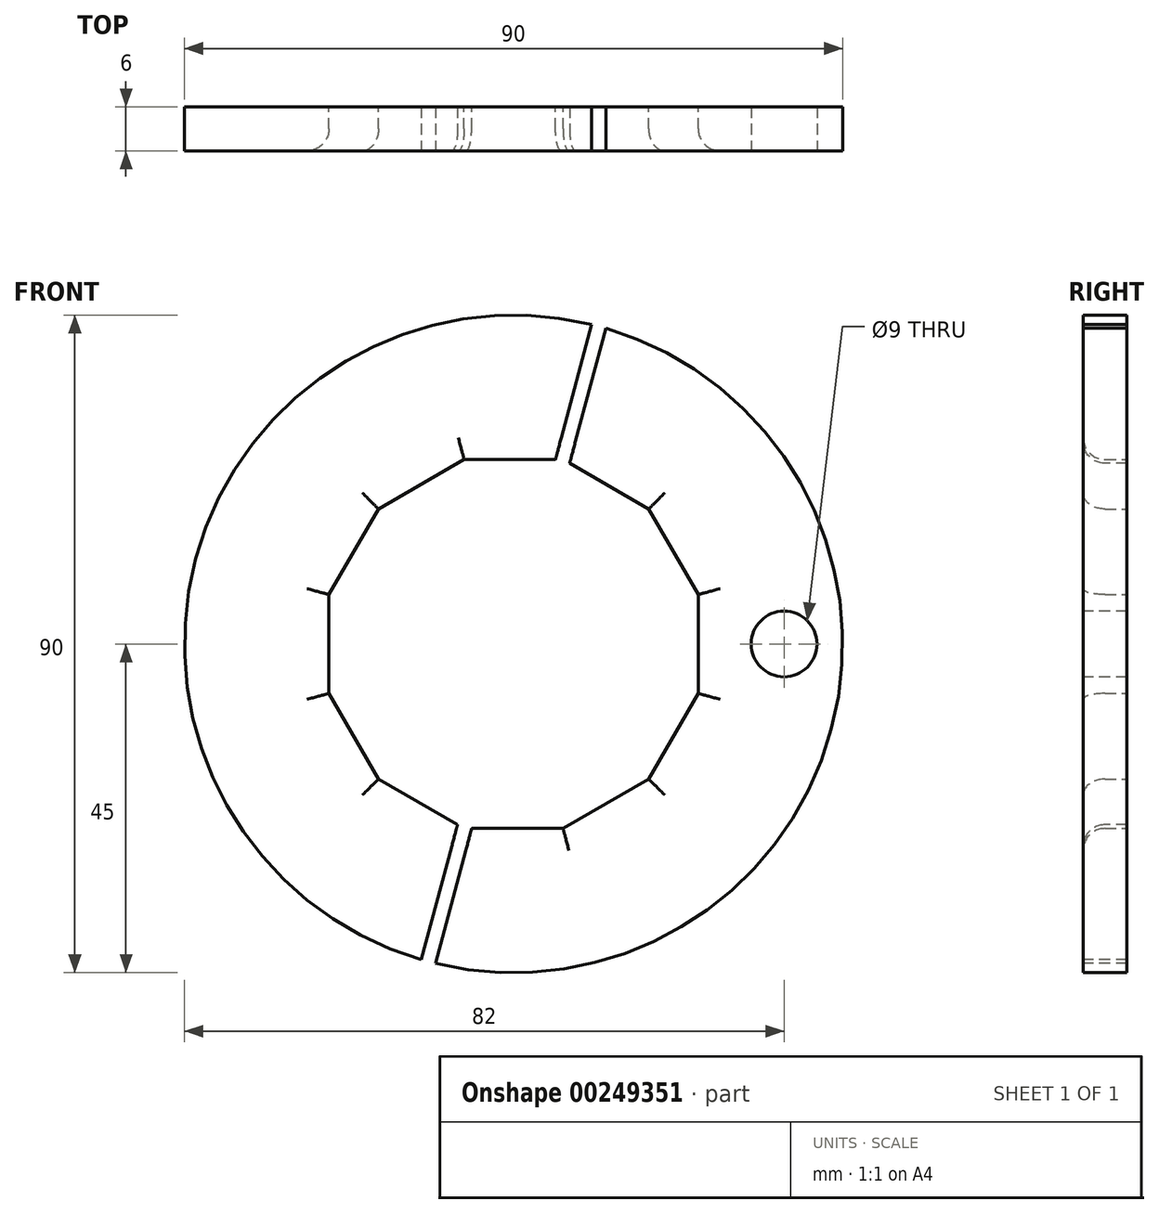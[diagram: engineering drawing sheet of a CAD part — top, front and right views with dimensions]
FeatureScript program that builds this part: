
annotation { "Feature Type Name" : "Feature", "Feature Type Description" : "" }
export const myFeature = defineFeature(function(context is Context, id is Id, definition is map)
    precondition{}
    {
        {
            var Q0;
            Q0=qCreatedBy(makeId("Front.planeOp"),FACE);
            var sketch = newSketch(context, id + "F0", { "sketchPlane" : qUnion([Q0])});
            skCircle(sketch, "E0.cCircle", {"center": v(0, 0) * mm, "radius": 25.25 * mm, "construction": true});
            skLineSegment(sketch, "E0.0", {"start": v(-6.77, 25.25) * mm, "end": v(6.77, 25.25) * mm});
            skLineSegment(sketch, "E0.1", {"start": v(6.77, 25.25) * mm, "end": v(18.48, 18.48) * mm});
            skLineSegment(sketch, "E0.2", {"start": v(18.48, 18.48) * mm, "end": v(25.25, 6.77) * mm});
            skLineSegment(sketch, "E0.3", {"start": v(25.25, 6.77) * mm, "end": v(25.25, -6.77) * mm});
            skLineSegment(sketch, "E0.4", {"start": v(25.25, -6.77) * mm, "end": v(18.48, -18.48) * mm});
            skLineSegment(sketch, "E0.5", {"start": v(18.48, -18.48) * mm, "end": v(6.77, -25.25) * mm});
            skLineSegment(sketch, "E0.6", {"start": v(6.77, -25.25) * mm, "end": v(-6.77, -25.25) * mm});
            skLineSegment(sketch, "E0.7", {"start": v(-6.77, -25.25) * mm, "end": v(-18.48, -18.48) * mm});
            skLineSegment(sketch, "E0.8", {"start": v(-18.48, -18.48) * mm, "end": v(-25.25, -6.77) * mm});
            skLineSegment(sketch, "E0.9", {"start": v(-25.25, -6.77) * mm, "end": v(-25.25, 6.77) * mm});
            skLineSegment(sketch, "E0.10", {"start": v(-25.25, 6.77) * mm, "end": v(-18.48, 18.48) * mm});
            skLineSegment(sketch, "E0.11", {"start": v(-18.48, 18.48) * mm, "end": v(-6.77, 25.25) * mm});
            skPoint(sketch, "E0.0.midPoint", {"position": v(0, 25.25) * mm});
            skCircle(sketch, "E1", {"center": v(0, 0) * mm, "radius": 45 * mm});
            skSolve(sketch);
        }
        {
            var Q0;
            Q0=makeQuery(id+"F0.imprint","IMPRINT",FACE,{"disambiguationData":[TD([[makeQuery(id+"F0.imprint","IMPRINT",EDGE,{"derivedFrom":sQuery(id+"F0.wireOp",EDGE,"E0.0")}),1.0]])]});
            extrude(context, id + "F1", {"entities" : qUnion([Q0]), "depth" : 6 * mm, "symmetric" : true});
        }
        {
            var Q0;
            Q0=makeQuery(id+"F1.opExtrude","CAP_EDGE",EDGE,{"disambiguationData":[OSD([sQuery(id+"F0.wireOp",EDGE,"E0.11")])],"isStart":false});
            var Q1;
            Q1=makeQuery(id+"F1.opExtrude","CAP_EDGE",EDGE,{"disambiguationData":[OSD([sQuery(id+"F0.wireOp",EDGE,"E0.0")])],"isStart":false});
            var Q2;
            Q2=makeQuery(id+"F1.opExtrude","CAP_EDGE",EDGE,{"disambiguationData":[OSD([sQuery(id+"F0.wireOp",EDGE,"E0.1")])],"isStart":false});
            var Q3;
            Q3=makeQuery(id+"F1.opExtrude","CAP_EDGE",EDGE,{"disambiguationData":[OSD([sQuery(id+"F0.wireOp",EDGE,"E0.2")])],"isStart":false});
            var Q4;
            Q4=makeQuery(id+"F1.opExtrude","CAP_EDGE",EDGE,{"disambiguationData":[OSD([sQuery(id+"F0.wireOp",EDGE,"E0.3")])],"isStart":false});
            var Q5;
            Q5=makeQuery(id+"F1.opExtrude","CAP_EDGE",EDGE,{"disambiguationData":[OSD([sQuery(id+"F0.wireOp",EDGE,"E0.4")])],"isStart":false});
            var Q6;
            Q6=makeQuery(id+"F1.opExtrude","CAP_EDGE",EDGE,{"disambiguationData":[OSD([sQuery(id+"F0.wireOp",EDGE,"E0.5")])],"isStart":false});
            var Q7;
            Q7=makeQuery(id+"F1.opExtrude","CAP_EDGE",EDGE,{"disambiguationData":[OSD([sQuery(id+"F0.wireOp",EDGE,"E0.6")])],"isStart":false});
            var Q8;
            Q8=makeQuery(id+"F1.opExtrude","CAP_EDGE",EDGE,{"disambiguationData":[OSD([sQuery(id+"F0.wireOp",EDGE,"E0.7")])],"isStart":false});
            var Q9;
            Q9=makeQuery(id+"F1.opExtrude","CAP_EDGE",EDGE,{"disambiguationData":[OSD([sQuery(id+"F0.wireOp",EDGE,"E0.8")])],"isStart":false});
            var Q10;
            Q10=makeQuery(id+"F1.opExtrude","CAP_EDGE",EDGE,{"disambiguationData":[OSD([sQuery(id+"F0.wireOp",EDGE,"E0.9")])],"isStart":false});
            var Q11;
            Q11=makeQuery(id+"F1.opExtrude","CAP_EDGE",EDGE,{"disambiguationData":[OSD([sQuery(id+"F0.wireOp",EDGE,"E0.10")])],"isStart":false});
            fillet(context, id + "F2", {"entities" : qUnion([Q0, Q1, Q2, Q3, Q4, Q5, Q6, Q7, Q8, Q9, Q10, Q11]), "radius" : 3 * mm, "tangentPropagation" : true, "allowEdgeOverflow" : false});
        }
        {
            var Q0;
            Q0=qCreatedBy(makeId("Front.planeOp"),FACE);
            var sketch = newSketch(context, id + "F3", { "sketchPlane" : qUnion([Q0])});
            skCircle(sketch, "E2", {"center": v(37, 0) * mm, "radius": 4.5 * mm});
            skSolve(sketch);
        }
        {
            var Q0;
            Q0=qSketchRegion(id+"F3",true);
            extrude(context, id + "F4", {"entities" : qUnion([Q0]), "operationType" : NewBodyOperationType.REMOVE, "oppositeDirection" : true, "depth" : 25 * mm, "symmetric" : true});
        }
        {
            var Q0;
            Q0=makeQuery(id+"F1.opExtrude","CAP_FACE",FACE,{"disambiguationData":[OSD([sQuery(id+"F0.wireOp",EDGE,"E0.0"),sQuery(id+"F0.wireOp",EDGE,"E0.1"),sQuery(id+"F0.wireOp",EDGE,"E0.2"),sQuery(id+"F0.wireOp",EDGE,"E0.3"),sQuery(id+"F0.wireOp",EDGE,"E0.4"),sQuery(id+"F0.wireOp",EDGE,"E0.5"),sQuery(id+"F0.wireOp",EDGE,"E0.6"),sQuery(id+"F0.wireOp",EDGE,"E0.7"),sQuery(id+"F0.wireOp",EDGE,"E0.8"),sQuery(id+"F0.wireOp",EDGE,"E0.9"),sQuery(id+"F0.wireOp",EDGE,"E0.10"),sQuery(id+"F0.wireOp",EDGE,"E0.11"),sQuery(id+"F0.wireOp",EDGE,"E1")])],"isStart":false});
            var sketch = newSketch(context, id + "F5", { "sketchPlane" : qUnion([Q0])});
            skLineSegment(sketch, "E3.0", {"start": v(-11.65, -43.47) * mm, "end": v(11.65, 43.47) * mm, "construction": true});
            skCircle(sketch, "E4.0", {"center": v(0, 0) * mm, "radius": 45 * mm, "construction": true});
            skPoint(sketch, "E5.orphan", {"position": v(7.57, 28.25) * mm});
            skPoint(sketch, "E6.orphan", {"position": v(6.77, 25.25) * mm});
            skLineSegment(sketch, "E7", {"start": v(-17.25, -60.52) * mm, "end": v(12.57, 50.77) * mm});
            skLineSegment(sketch, "E8", {"start": v(12.57, 50.77) * mm, "end": v(14.5, 50.25) * mm});
            skLineSegment(sketch, "E9", {"start": v(14.5, 50.25) * mm, "end": v(-15.32, -61.04) * mm});
            skLineSegment(sketch, "E10", {"start": v(-15.32, -61.04) * mm, "end": v(-17.25, -60.52) * mm});
            skSolve(sketch);
        }
        {
            var Q0;
            {var subQ0=sQuery(id+"F0.wireOp",EDGE,"E1");var subQ7=sQuery(id+"F5.wireOp",EDGE,"E7");var subQ10=makeQuery(id+"F1.opExtrude","CAP_EDGE",EDGE,{"disambiguationData":[OSD([subQ0])],"isStart":false});var subQ13=makeQuery(id+"F5.imprint","INTERSECT",VERTEX,{"disambiguationData":[OD(0.0)],"derivedFrom":[subQ10,subQ7]});Q0=makeQuery(id+"F5.imprint","IMPRINT",FACE,{"disambiguationData":[TD([[makeQuery(id+"F5.imprint","IMPRINT",EDGE,{"disambiguationData":[TD([[subQ13,-1.0]])],"derivedFrom":subQ10}),1.0]])]});}
            var Q1;
            {var subQ0=sQuery(id+"F0.wireOp",EDGE,"E1");var subQ7=sQuery(id+"F5.wireOp",EDGE,"E7");var subQ9=makeQuery(id+"F1.opExtrude","CAP_EDGE",EDGE,{"disambiguationData":[OSD([subQ0])],"isStart":false});var subQ10=makeQuery(id+"F5.imprint","INTERSECT",VERTEX,{"disambiguationData":[OD(1.0)],"derivedFrom":[subQ9,subQ7]});Q1=makeQuery(id+"F5.imprint","IMPRINT",FACE,{"disambiguationData":[TD([[makeQuery(id+"F5.imprint","IMPRINT",EDGE,{"disambiguationData":[TD([[subQ10,1.0]])],"derivedFrom":subQ9}),1.0]])]});}
            var Q2;
            {var subQ0=sQuery(id+"F0.wireOp",EDGE,"E0.7");var subQ1=sQuery(id+"F0.wireOp",EDGE,"E0.6");var subQ2=sQuery(id+"F0.wireOp",EDGE,"E0.1");var subQ3=sQuery(id+"F0.wireOp",EDGE,"E0.0");var subQ4=makeQuery(id+"F1.opExtrude","CAP_FACE",FACE,{"disambiguationData":[OSD([subQ3,subQ2,sQuery(id+"F0.wireOp",EDGE,"E0.2"),sQuery(id+"F0.wireOp",EDGE,"E0.3"),sQuery(id+"F0.wireOp",EDGE,"E0.4"),sQuery(id+"F0.wireOp",EDGE,"E0.5"),subQ1,subQ0,sQuery(id+"F0.wireOp",EDGE,"E0.8"),sQuery(id+"F0.wireOp",EDGE,"E0.9"),sQuery(id+"F0.wireOp",EDGE,"E0.10"),sQuery(id+"F0.wireOp",EDGE,"E0.11"),sQuery(id+"F0.wireOp",EDGE,"E1")])],"isStart":false});var subQ8=sQuery(id+"F5.wireOp",EDGE,"E7");var subQ14=makeQuery(id+"F2.opFillet","BLEND_EDGE",EDGE,{"blendedFrom":[makeQuery(id+"F1.opExtrude","CAP_EDGE",EDGE,{"disambiguationData":[OSD([subQ0])],"isStart":false}),subQ4],"blendedInto":[subQ4]});var subQ15=makeQuery(id+"F5.imprint","INTERSECT",VERTEX,{"derivedFrom":[subQ14,subQ8]});Q2=makeQuery(id+"F5.imprint","IMPRINT",FACE,{"disambiguationData":[TD([[makeQuery(id+"F5.imprint","IMPRINT",EDGE,{"disambiguationData":[TD([[subQ15,-1.0]])],"derivedFrom":subQ8}),-1.0]])]});}
            extrude(context, id + "F6", {"entities" : qUnion([Q0, Q1, Q2]), "operationType" : NewBodyOperationType.REMOVE, "oppositeDirection" : true, "depth" : 25 * mm});
        }
    });
